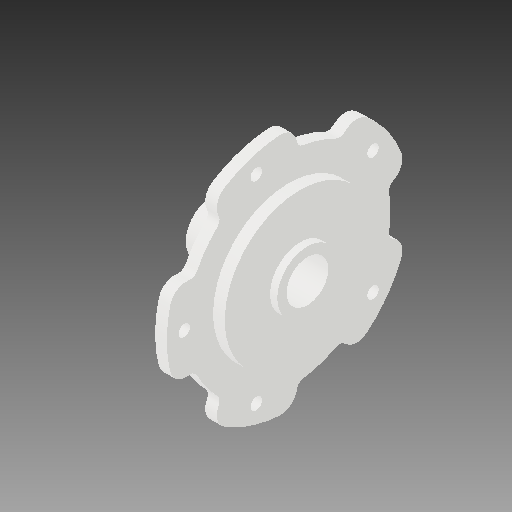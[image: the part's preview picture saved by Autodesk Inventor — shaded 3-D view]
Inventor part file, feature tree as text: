
AUTODESK INVENTOR PART (.ipt)
format: ipt  version: 2019 (Build 230136000, 136)  size: 248,832 bytes
history: native  units: in
note: dims shown in document units (in); Inventor stores cm internally (conversion verified against a paired STEP export)
features: extrude x6, sketch x6, fillet x1, pattern_circular x1
ambient origin geometry x8: Origin, YZ Plane, XZ Plane, XY Plane, X Axis, Y Axis, Z Axis, Center Point
bodies: Solid1 (feature_tree)
feature tree (14):
  extrude  "Extrusion1"  Depth=0.1969in
  extrude  "Extrusion2"  Depth=1.0949in TaperAngle=0.0deg
  fillet  "Fillet1"  Radius=0.5512in
  extrude  "Extrusion3"  Depth=0.1969in TaperAngle=0.0deg
  extrude  "Extrusion4"  Depth=0.1224in TaperAngle=0.0deg
  extrude  "Extrusion5"  Depth=0.1224in
  extrude  "Extrusion6"  Depth=0.3937in TaperAngle=0.0deg
  pattern_circular  "Circular Pattern1"  Count=5 Angle=360.0deg
  sketch  "Sketch2"  dims[d53=0.1969in d54=0.0in d55=0.9055in]
  sketch  "Sketch3"  dims[d56=0.7087in d57=1.0949in d58=0.0in d59=0.5512in]
  sketch  "Sketch4"  dims[d60=2.5591in d61=0.1969in d62=0.0in]
  sketch  "Sketch5"  dims[d63=1.0236in d64=0.1224in d65=0.0in]
  sketch  "Sketch6"  dims[d66=0.1224in d67=0.0in d68=1.7717in]
  sketch  "Sketch7"  dims[d69=0.1969in d70=0.3937in d71=0.0in d72=1.9685in d73=360.0deg d75=2.0669in d76=0.2756in d77=0.128in d78=1.9685in d80=360.0deg d83=1.7323in d84=0.4921in d85=0.7677in]
